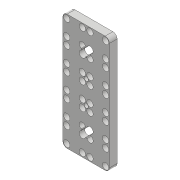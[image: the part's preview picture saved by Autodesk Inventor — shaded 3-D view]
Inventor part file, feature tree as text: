
AUTODESK INVENTOR PART (.ipt)
format: ipt  version: 2018 (Build 220112000, 112)  size: 743,936 bytes
history: native  units: mm
features: projected_geometry x10, extrude x9, sketch x8, pattern_linear x6, fillet x5
ambient origin geometry x8: Origin, YZ Plane, XZ Plane, XY Plane, X Axis, Y Axis, Z Axis, Center Point
bodies: Solid1 (feature_tree)
feature tree (38):
  extrude  "Extrusion1"  Depth=44.0mm
  extrude  "Extrusion2"  Depth=22.0mm
  extrude  "Extrusion3"  Depth=22.0mm
  pattern_linear  "Rectangular Pattern1"  Spacing1=6.0mm  [1 undecoded]
  extrude  "Extrusion4"  Depth=6.0mm
  pattern_linear  "Rectangular Pattern2"  Count1=5 Spacing1=22.0mm
  extrude  "Extrusion5"  Depth=22.0mm
  pattern_linear  "Rectangular Pattern3"  Spacing1=10.0mm  [1 undecoded]
  fillet  "Fillet1"  Radius=5.0mm
  extrude  "Extrusion6"  Depth=5.0mm
  extrude  "Extrusion9"  Depth=5.0mm
  pattern_linear  "Rectangular Pattern4"  Spacing1=2.0mm  [1 undecoded]
  extrude  "Extrusion7"  Depth=50.0mm
  pattern_linear  "Rectangular Pattern5"  Spacing1=2.0mm  [1 undecoded]
  pattern_linear  "Rectangular Pattern6"  Count1=2 Spacing1=22.0mm
  fillet  "Fillet2"  Radius=1.0mm
  fillet  "Fillet3"  Radius=8.5mm
  fillet  "Fillet4"  Radius=6.7mm
  extrude  "Extrusion8"  Depth=66.0mm
  fillet  "Fillet5"  Radius=4.0mm
  sketch  "Sketch1"  dims[d0=110.0mm d1=44.0mm]
  sketch  "Sketch2"  dims[d2=7.3mm d3=0.0mm d4=22.0mm]
  projected_geometry  "Projected Loop1"
  sketch  "Sketch3"  dims[d5=22.0mm d6=14.75mm]
  projected_geometry  "Projected Loop2"
  projected_geometry  "Projected Loop3"
  projected_geometry  "Projected Loop4"
  projected_geometry  "Projected Loop5"
  sketch  "Sketch4"  dims[d7=7.5mm]
  projected_geometry  "Projected Loop6"
  sketch  "Sketch5"  dims[d8=7.0mm d9=0.0mm]
  projected_geometry  "Projected Loop7"
  projected_geometry  "Projected Loop8"
  sketch  "Sketch7"  dims[d10=6.7mm d11=0.0mm]
  projected_geometry  "Projected Loop9"
  sketch  "Sketch8"  dims[d12=6.0mm]
  projected_geometry  "Projected Loop10"
  sketch  "Sketch9"  dims[d13=6.0mm d14=6.0mm d15=6.0mm d16=50.0mm d18=22.0mm d19=20.0mm d21=22.0mm d22=10.0mm d23=5.0mm d24=5.0mm d25=5.0mm d26=2.0mm d27=0.0mm d28=50.0mm d30=22.0mm d31=2.0mm d32=0.0mm d33=20.0mm d35=22.0mm d36=1.0mm d37=8.5mm d38=6.7mm d39=0.0mm d40=20.0mm d42=66.0mm d43=4.0mm d44=2.0mm d45=0.0mm d46=20.0mm d48=22.0mm d49=4.0mm d50=0.5mm d51=1.0mm d52=2.5mm d53=3.0mm d54=0.0mm d55=0.5mm d56=2.0mm d57=2.0mm d58=2.0mm d59=2.0mm d60=2.0mm d61=2.0mm d62=2.0mm d63=2.0mm d64=10.0mm d65=0.0mm d66=40.0mm d68=22.0mm]
note: 4 required parameter values undecoded (feature->parameter linkage not recoverable at this tier; creation-order binding heuristic only, values carry confidence <= 0.55)
